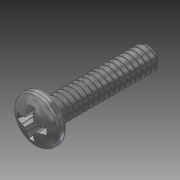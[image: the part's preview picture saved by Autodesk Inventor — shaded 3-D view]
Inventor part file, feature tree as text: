
AUTODESK INVENTOR PART (.ipt)
format: ipt  version: 2014 SP1 (Build 180222100, 222)  size: 724,992 bytes
history: native  units: in
note: dims shown in document units (in); Inventor stores cm internally (conversion verified against a paired STEP export)
features: fillet x1, other x1, imported_body x1
ambient origin geometry x8: Origin, YZ Plane, XZ Plane, XY Plane, X Axis, Y Axis, Z Axis, Center Point
bodies: Body1 (feature_tree)
feature tree (3):
  fillet  "Fillet1"  [1 undecoded]
  other  "91772A1501"
  imported_body  "Base1"
note: 1 required parameter value undecoded (feature->parameter linkage not recoverable at this tier; creation-order binding heuristic only, values carry confidence <= 0.55)
